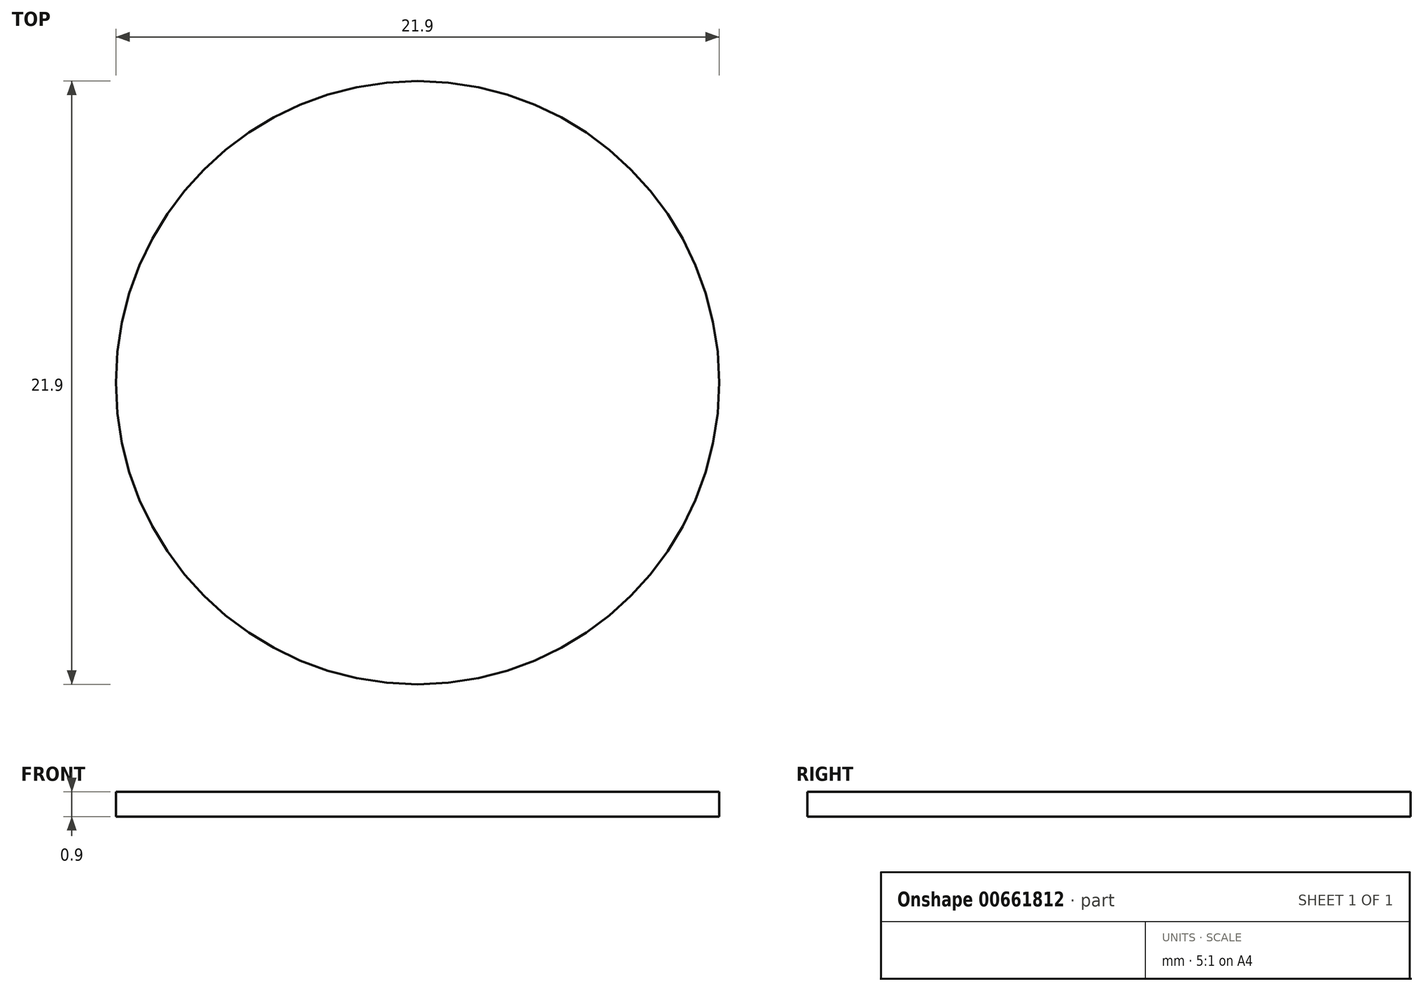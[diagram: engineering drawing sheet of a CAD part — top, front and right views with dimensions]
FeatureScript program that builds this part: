
annotation { "Feature Type Name" : "Feature", "Feature Type Description" : "" }
export const myFeature = defineFeature(function(context is Context, id is Id, definition is map)
    precondition{}
    {
        {
            var Q0;
            Q0=qCreatedBy(makeId("Top.planeOp"),FACE);
            var sketch = newSketch(context, id + "F0", { "sketchPlane" : qUnion([Q0])});
            skCircle(sketch, "E0", {"center": v(0, 0) * mm, "radius": 10.95 * mm});
            skSolve(sketch);
        }
        {
            var Q0;
            Q0 = qSketchRegion(id + "F0", true);
            extrude(context, id + "F1", {"entities" : qUnion([Q0]), "depth" : .9 * mm, "offsetDistance" : 25 * mm});
        }
    });
